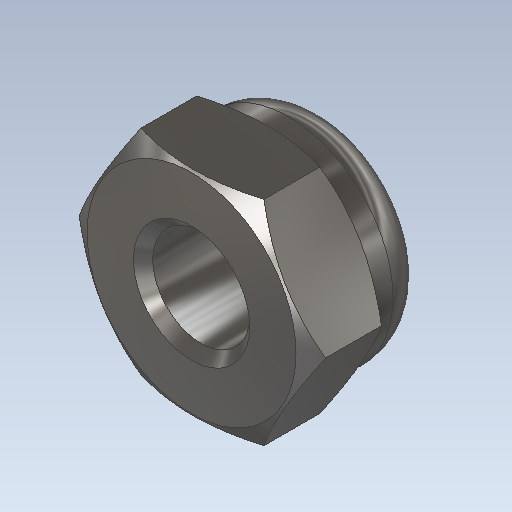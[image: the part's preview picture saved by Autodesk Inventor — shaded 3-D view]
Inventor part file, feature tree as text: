
AUTODESK INVENTOR PART (.ipt)
format: ipt  version: 2020.1 (Build 241239000, 239)  size: 235,008 bytes
history: native  units: mm
features: sketch x4, extrude x3, fillet x2, other x1, revolve x1, chamfer x1
ambient origin geometry x8: Origin, YZ Plane, XZ Plane, XY Plane, X Axis, Y Axis, Z Axis, Center Point
bodies: Body1 (feature_tree)
feature tree (12):
  other  "Твердое тело1"
  extrude  "Выдавливание1"  Depth=4.0mm TaperAngle=0.0deg
  revolve  "Вращение1"
  extrude  "Выдавливание2"  TaperAngle=60.0deg  [1 undecoded]
  fillet  "Сопряжение1"  Radius=1.0mm
  chamfer  "Фаска2"  Distance=3.5mm
  extrude  "Extrusion4"  TaperAngle=90.0deg  [1 undecoded]
  fillet  "Fillet3"  Radius=3.0mm
  sketch  "Эскиз1"
  sketch  "Эскиз2"
  sketch  "Эскиз3"
  sketch  "Sketch5"  dims[d0=5.0mm d2=4.0mm d3=0.0mm d4=60.0deg d5=1.0mm d6=3.5mm d7=90.0deg d8=3.0mm d9=0.0mm d10=2.0mm d18=0.5mm d19=2.0mm d20=45.0deg d21=3.0mm d22=0.2mm d23=0.0mm d24=0.2mm]
note: 2 required parameter values undecoded (feature->parameter linkage not recoverable at this tier; creation-order binding heuristic only, values carry confidence <= 0.55)
